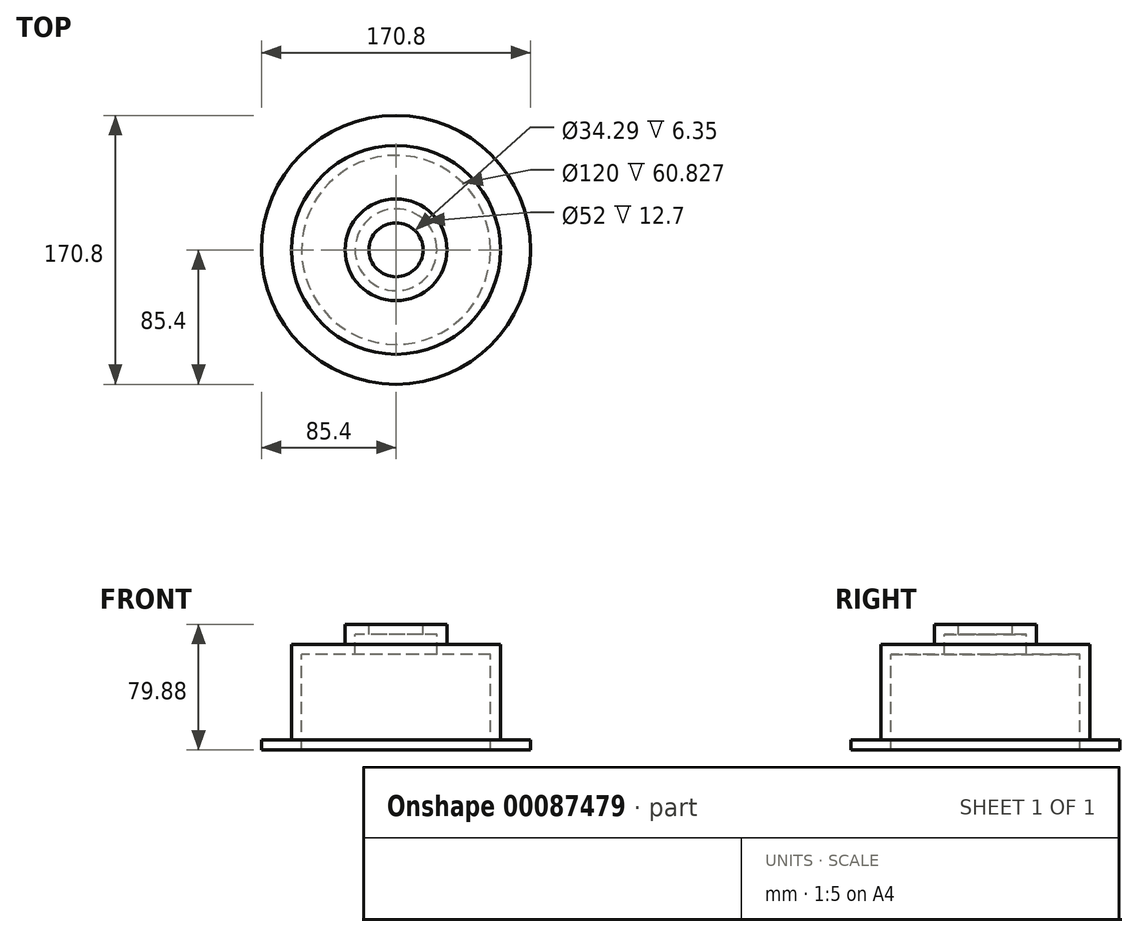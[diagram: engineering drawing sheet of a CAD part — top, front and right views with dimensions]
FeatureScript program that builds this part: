
annotation { "Feature Type Name" : "Feature", "Feature Type Description" : "" }
export const myFeature = defineFeature(function(context is Context, id is Id, definition is map)
    precondition{}
    {
        {
            var Q0;
            Q0=qCreatedBy(makeId("Front.planeOp"),FACE);
            var sketch = newSketch(context, id + "F0", { "sketchPlane" : qUnion([Q0])});
            skLineSegment(sketch, "E0", {"start": v(-17.15, 0) * mm, "end": v(-26, 0) * mm});
            skLineSegment(sketch, "E1", {"start": v(-26, 0) * mm, "end": v(-26, -12.7) * mm});
            skLineSegment(sketch, "E2", {"start": v(-26, -12.7) * mm, "end": v(-60, -12.7) * mm});
            skLineSegment(sketch, "E3", {"start": v(-60, -12.7) * mm, "end": v(-60, -73.53) * mm});
            skLineSegment(sketch, "E4", {"start": v(-60, -73.53) * mm, "end": v(-85.4, -73.53) * mm});
            skLineSegment(sketch, "E5.0", {"start": v(-66.35, -67.18) * mm, "end": v(-85.4, -67.18) * mm});
            skLineSegment(sketch, "E5.1", {"start": v(-17.15, 6.35) * mm, "end": v(-32.35, 6.35) * mm});
            skLineSegment(sketch, "E5.2", {"start": v(-32.35, 6.35) * mm, "end": v(-32.35, -6.35) * mm});
            skLineSegment(sketch, "E5.3", {"start": v(-32.35, -6.35) * mm, "end": v(-66.35, -6.35) * mm});
            skLineSegment(sketch, "E5.4", {"start": v(-66.35, -6.35) * mm, "end": v(-66.35, -67.18) * mm});
            skLineSegment(sketch, "E6", {"start": v(-17.15, 6.35) * mm, "end": v(-17.15, 0) * mm});
            skLineSegment(sketch, "E7", {"start": v(-85.4, -67.18) * mm, "end": v(-85.4, -73.53) * mm});
            skLineSegment(sketch, "E8", {"start": v(0, 32.3) * mm, "end": v(0, -87.06) * mm, "construction": true});
            skSolve(sketch);
        }
        {
            var Q0;
            Q0 = qSketchRegion(id + "F0", true);
            var Q1;
            Q1=sQuery(id+"F0.wireOp",EDGE,"E8");
            revolve(context, id + "F1", {"entities" : qUnion([Q0]), "axis" : qUnion([Q1]), "revolveType" : RevolveType.FULL});
        }
    });
